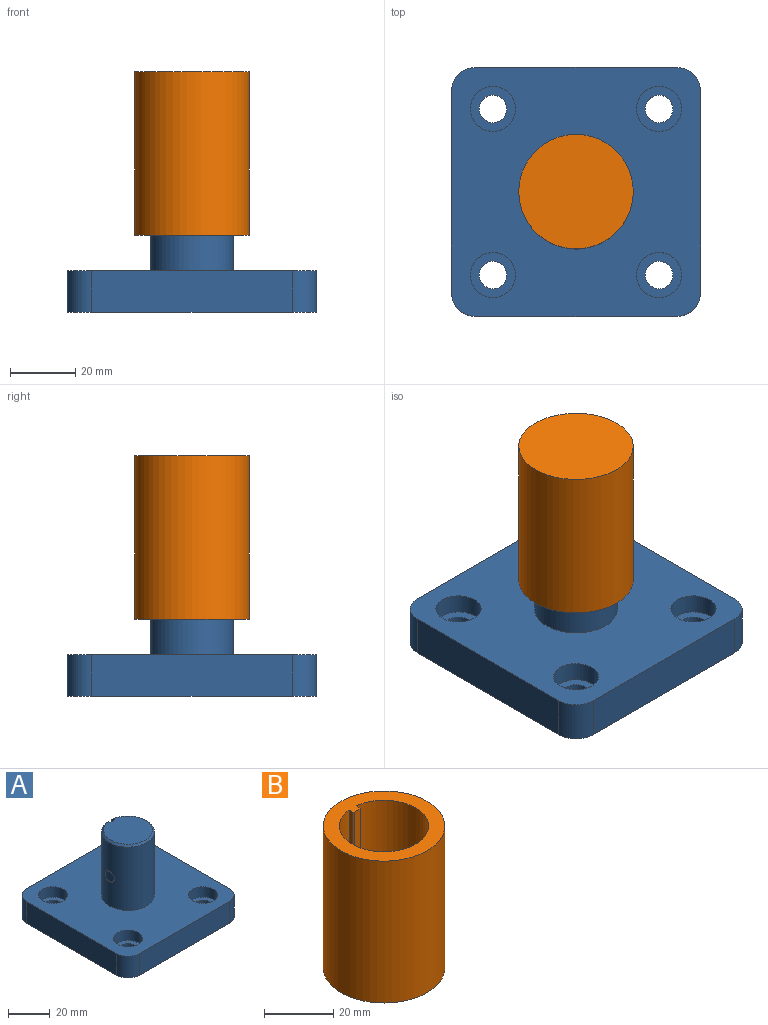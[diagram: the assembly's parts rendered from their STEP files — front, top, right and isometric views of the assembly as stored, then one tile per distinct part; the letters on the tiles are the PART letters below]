
ASSEMBLY  parts=2 mates=2
PART A: 32 faces, bbox 76.2x76.2x50.8 mm
  f0: cylinder r=12.7mm len=6.25mm, axis (0,0,-1), area 29.6mm2, adj f1
  f1: bspline ~6.25x6mm, area 13.1mm2, adj f0,f2
  f2: cylinder r=2.5mm len=24.4mm, axis (1,0,0), area 383.3mm2, adj f1,f3
  f3: bspline ~6.25x6mm, area 13.1mm2, adj f2,f4
  f4: cylinder r=12.7mm len=37.1mm, axis (0,0,-1), area 2819.3mm2, adj f3,f5,f29,f30,f31
  f5: plane 76.2x76.2mm, normal (0,0,1), area 4659.1mm2, adj f4,f6,f16,f17,f18,f19,f20,f21
  f6: cylinder r=7.5mm len=12.7mm, axis (0,0,-1), area 149.6mm2, adj f5,f7,f16,f22
  f7: plane 76.2x76.2mm, normal (0,0,-1), area 5536.5mm2, adj f6,f8,f10,f12,f14,f16,f17,f18
  f8: cylinder r=4.2mm len=8.4mm, axis (0,0,1), area 176.8mm2, adj f7,f9
  f9: plane 13.8x13.8mm, normal (0,0,1), area 94.2mm2, adj f8,f23
  f10: cylinder r=4.2mm len=8.4mm, axis (0,0,1), area 176.8mm2, adj f7,f11
  f11: plane 13.8x13.8mm, normal (0,0,1), area 94.2mm2, adj f10,f24
  f12: cylinder r=4.2mm len=8.4mm, axis (0,0,1), area 176.8mm2, adj f7,f13
  f13: plane 13.8x13.8mm, normal (0,0,1), area 94.2mm2, adj f12,f25
  f14: cylinder r=4.2mm len=8.4mm, axis (0,0,1), area 176.8mm2, adj f7,f15
  f15: plane 13.8x13.8mm, normal (0,0,1), area 94.2mm2, adj f14,f26
  f16: plane 61.2x12.7mm, normal (0,-1,0), area 777.2mm2, adj f5,f6,f7,f17
  f17: cylinder r=7.5mm len=12.7mm, axis (0,0,1), area 149.6mm2, adj f5,f7,f16,f18
  f18: plane 61.2x12.7mm, normal (-1,0,0), area 777.2mm2, adj f5,f7,f17,f19
  f19: cylinder r=7.5mm len=12.7mm, axis (0,0,-1), area 149.6mm2, adj f5,f7,f18,f20
  f20: plane 61.2x12.7mm, normal (0,1,0), area 777.2mm2, adj f5,f7,f19,f21
  f21: cylinder r=7.5mm len=12.7mm, axis (0,0,1), area 149.6mm2, adj f5,f7,f20,f22
  f22: plane 61.2x12.7mm, normal (1,0,0), area 777.2mm2, adj f5,f6,f7,f21
  f23: cylinder r=6.9mm len=13.8mm, axis (0,0,1), area 260.1mm2, adj f5,f9
  f24: cylinder r=6.9mm len=13.8mm, axis (0,0,1), area 260.1mm2, adj f5,f11
  f25: cylinder r=6.9mm len=13.8mm, axis (0,0,1), area 260.1mm2, adj f5,f13
  f26: cylinder r=6.9mm len=13.8mm, axis (0,0,1), area 260.1mm2, adj f5,f15
  f27: plane 38.1x3mm, normal (0,1,0), area 114.3mm2, adj f5,f28,f29,f31
  f28: plane 23.4x23.3mm, normal (0,0,1), area 427.1mm2, adj f27,f29,f30,f31
  f29: plane 38.11x1.92mm, normal (1,0,0), area 72.3mm2, adj f4,f5,f27,f28,f30
  f30: cone r=11.7mm half-angle=45deg, axis (0,0,-1), area 104.1mm2, adj f4,f28,f29,f31
  f31: plane 38.11x1.92mm, normal (-1,0,0), area 72.3mm2, adj f4,f5,f27,f28,f30
PART B: 10 faces, bbox 35x35x50 mm
  f0: cylinder r=12.85mm len=38.1mm, axis (0,0,1), area 2965.4mm2, adj f1,f3,f5,f6
  f1: plane 25.7x25.62mm, normal (0,0,1), area 513.4mm2, adj f0,f5,f6,f7,f8,f9
  f2: cylinder r=17.5mm len=50mm, axis (0,0,-1), area 5497.8mm2, adj f3,f4
  f3: plane 35x35mm, normal (0,0,1), area 448.7mm2, adj f0,f2,f5,f6,f7,f8,f9
  f4: plane 35x35mm, normal (0,0,-1), area 962.1mm2, adj f2
  f5: plane 38.1x1.57mm, normal (-1,0,0), area 59.7mm2, adj f0,f1,f3,f8
  f6: plane 38.1x1.57mm, normal (1,0,0), area 59.7mm2, adj f0,f1,f3,f9
  f7: plane 38.1x2.4mm, normal (0,-1,0), area 91.4mm2, adj f1,f3,f8,f9
  f8: plane 38.1x0.25mm, normal (-0.71,-0.71,0), area 13.5mm2, adj f1,f3,f5,f7
  f9: plane 38.1x0.25mm, normal (0.71,-0.71,0), area 13.5mm2, adj f1,f3,f6,f7
PLACE A t=(-25.04,7.97,8.24)mm fixed
PLACE B rot(axis=(0,1,0),180deg) t=(-25.04,7.97,81.82)mm
MATE cylindrical A.f0 <-> B.f0  axis (0,0,-1) through (-25.04,7.97,39.49)mm
MATE parallel A.f29 <-> B.f6  axis (1,0,0) through (-26.54,19.62,39.86)mm
